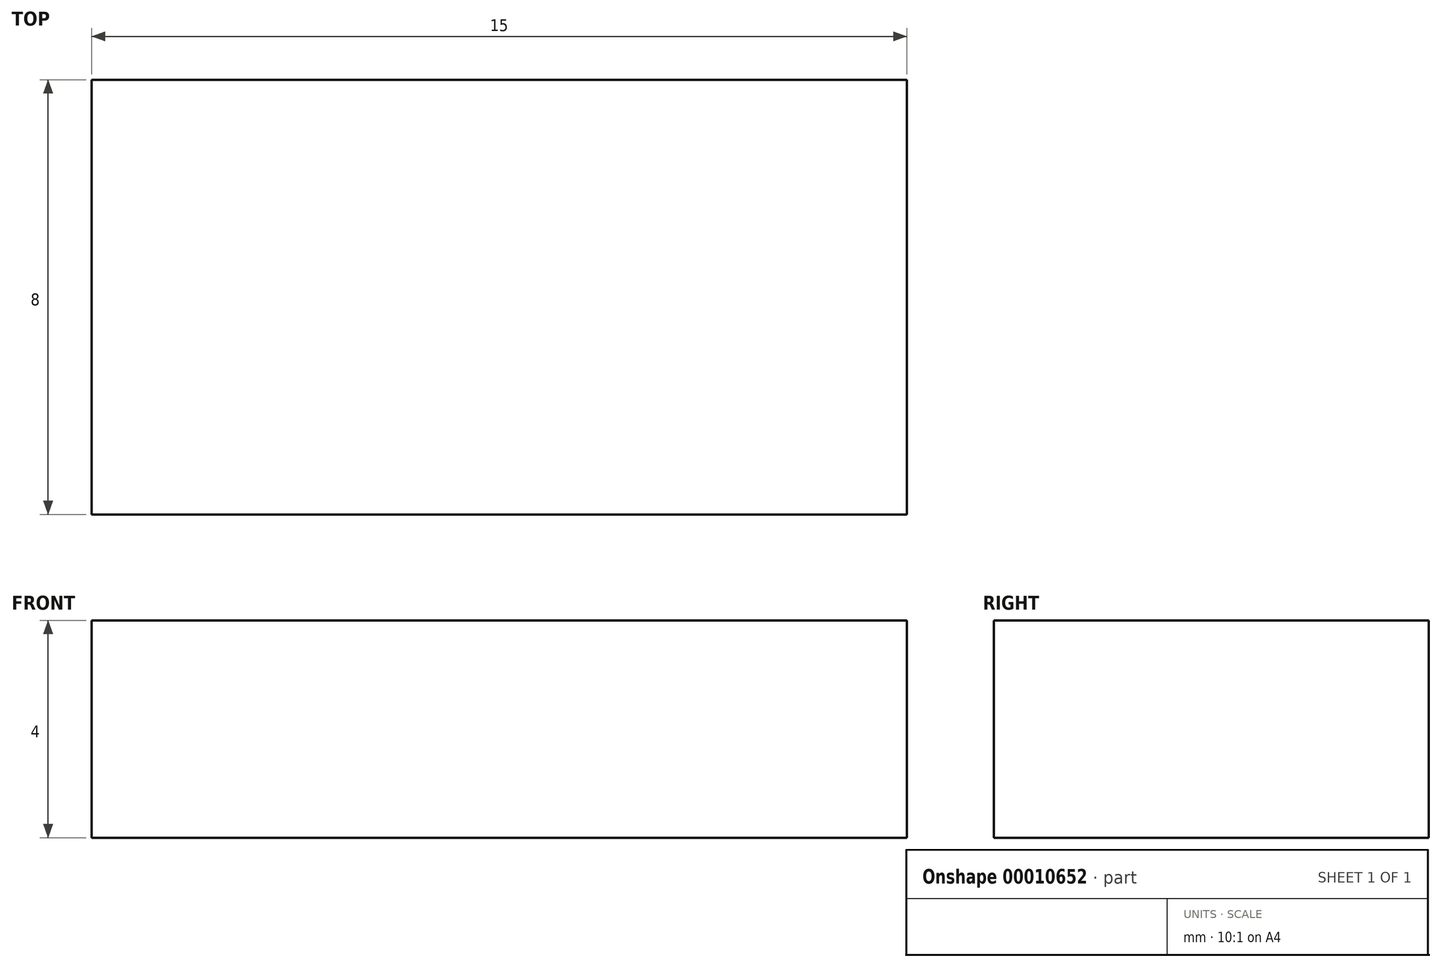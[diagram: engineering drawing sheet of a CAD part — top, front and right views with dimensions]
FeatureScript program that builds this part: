
annotation { "Feature Type Name" : "Feature", "Feature Type Description" : "" }
export const myFeature = defineFeature(function(context is Context, id is Id, definition is map)
    precondition{}
    {
        {
            var Q0;
            Q0=qCreatedBy(makeId("Top.planeOp"),FACE);
            var sketch = newSketch(context, id + "F0", { "sketchPlane" : qUnion([Q0])});
            skLineSegment(sketch, "E0.bottom", {"start": v(0, 0) * mm, "end": v(-15, 0) * mm});
            skLineSegment(sketch, "E0.top", {"start": v(0, -8) * mm, "end": v(-15, -8) * mm});
            skLineSegment(sketch, "E0.left", {"start": v(0, 0) * mm, "end": v(0, -8) * mm});
            skLineSegment(sketch, "E0.right", {"start": v(-15, 0) * mm, "end": v(-15, -8) * mm});
            skSolve(sketch);
        }
        {
            var Q0;
            Q0=makeQuery(id+"F0.imprint","IMPRINT",FACE,{"disambiguationData":[TD([[makeQuery(id+"F0.imprint","IMPRINT",EDGE,{"derivedFrom":sQuery(id+"F0.wireOp",EDGE,"E0.bottom")}),1.0]])]});
            extrude(context, id + "F1", {"entities" : qUnion([Q0]), "depth" : 4 * mm});
        }
    });
